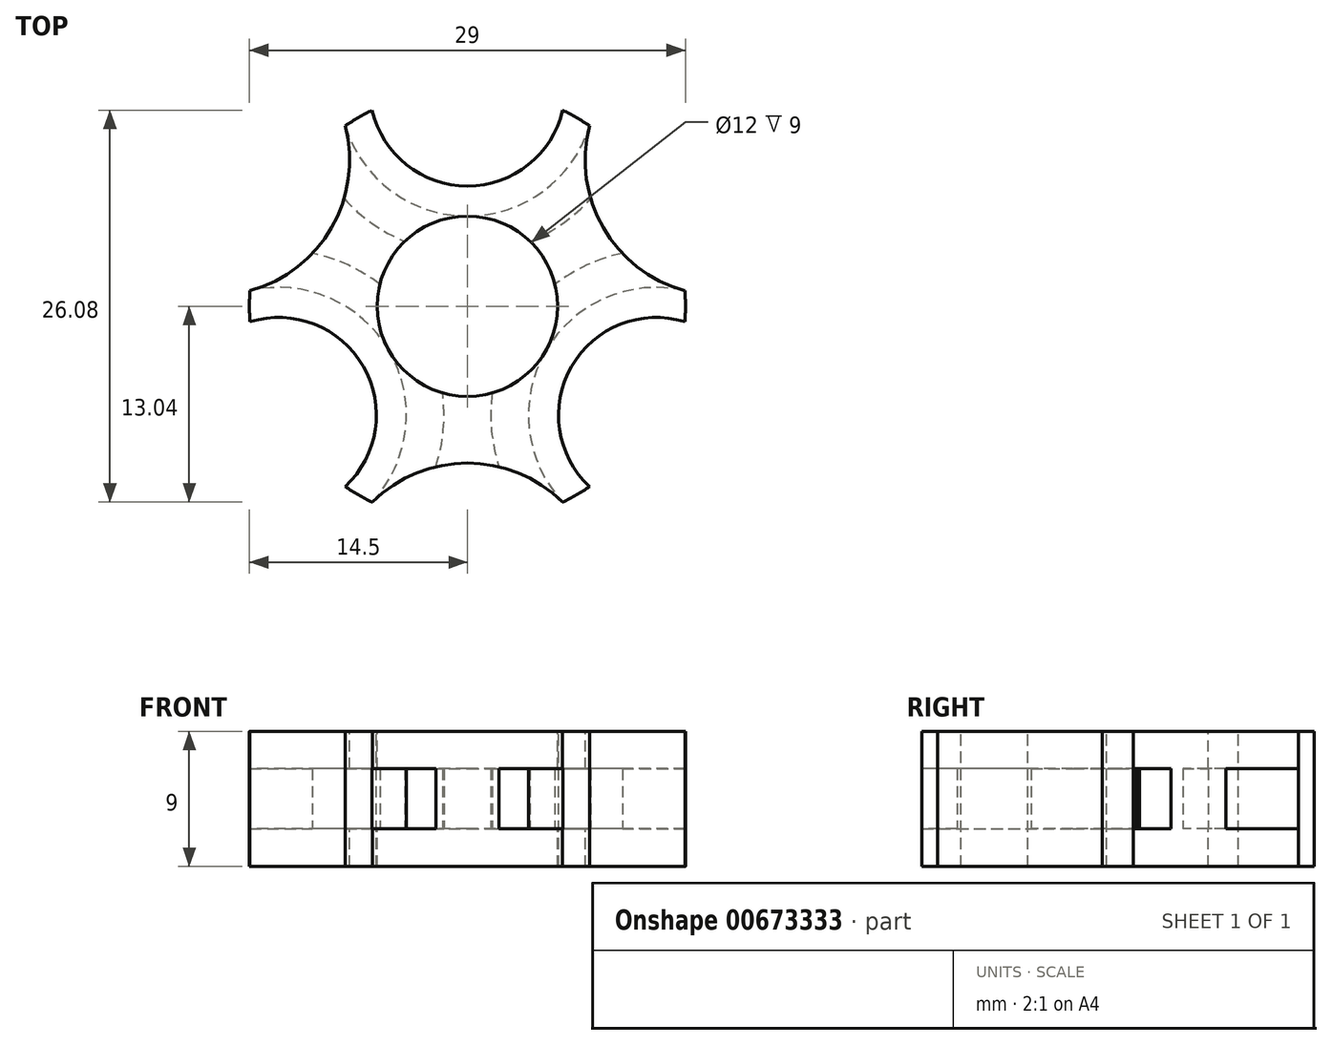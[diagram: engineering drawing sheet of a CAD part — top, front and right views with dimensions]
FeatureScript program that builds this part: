
annotation { "Feature Type Name" : "Feature", "Feature Type Description" : "" }
export const myFeature = defineFeature(function(context is Context, id is Id, definition is map)
    precondition{}
    {
        {
            var Q0;
            Q0=qCreatedBy(makeId("Top.planeOp"),FACE);
            var sketch = newSketch(context, id + "F0", { "sketchPlane" : qUnion([Q0])});
            skCircle(sketch, "E0", {"center": v(0, 0) * mm, "radius": 6 * mm});
            skCircle(sketch, "E1", {"center": v(0, 14.5) * mm, "radius": 8.5 * mm});
            skCircle(sketch, "E2", {"center": v(-12.56, -7.25) * mm, "radius": 8.5 * mm});
            skCircle(sketch, "E3", {"center": v(12.56, -7.25) * mm, "radius": 8.5 * mm});
            skLineSegment(sketch, "E4", {"start": v(0, 14.5) * mm, "end": v(-12.56, -7.25) * mm, "construction": true});
            skLineSegment(sketch, "E5", {"start": v(12.56, -7.25) * mm, "end": v(-12.56, -7.25) * mm, "construction": true});
            skLineSegment(sketch, "E6", {"start": v(0, 14.5) * mm, "end": v(12.56, -7.25) * mm, "construction": true});
            skCircle(sketch, "E7", {"center": v(0, 14.5) * mm, "radius": 6.5 * mm});
            skCircle(sketch, "E8", {"center": v(12.56, -7.25) * mm, "radius": 6.5 * mm});
            skCircle(sketch, "E9", {"center": v(-12.56, -7.25) * mm, "radius": 6.5 * mm});
            skCircle(sketch, "E10", {"center": v(0, 0) * mm, "radius": 14.5 * mm});
            skCircle(sketch, "E11", {"center": v(-16.83, 9.72) * mm, "radius": 9 * mm});
            skCircle(sketch, "E12", {"center": v(16.83, 9.72) * mm, "radius": 9 * mm});
            skCircle(sketch, "E13", {"center": v(0, -19.44) * mm, "radius": 9 * mm});
            skCircle(sketch, "E14", {"center": v(0, 14.5) * mm, "radius": 11 * mm});
            skCircle(sketch, "E15", {"center": v(12.56, -7.25) * mm, "radius": 11 * mm});
            skCircle(sketch, "E16", {"center": v(-12.56, -7.25) * mm, "radius": 11 * mm});
            skSolve(sketch);
        }
        {
            var Q0;
            {var subQ1=sQuery(id+"F0.wireOp",EDGE,"E2");var subQ5=makeQuery(id+"F0.imprint","INTERSECT",VERTEX,{"derivedFrom":[sQuery(id+"F0.wireOp",EDGE,"E0"),subQ1]});Q0=makeQuery(id+"F0.imprint","IMPRINT",FACE,{"disambiguationData":[TD([[makeQuery(id+"F0.imprint","IMPRINT",EDGE,{"disambiguationData":[TD([[subQ5,-1.0]])],"derivedFrom":subQ1}),1.0]])]});}
            var Q1;
            {var subQ1=sQuery(id+"F0.wireOp",EDGE,"E3");var subQ6=makeQuery(id+"F0.imprint","INTERSECT",VERTEX,{"derivedFrom":[sQuery(id+"F0.wireOp",EDGE,"E0"),subQ1]});Q1=makeQuery(id+"F0.imprint","IMPRINT",FACE,{"disambiguationData":[TD([[makeQuery(id+"F0.imprint","IMPRINT",EDGE,{"disambiguationData":[TD([[subQ6,1.0]])],"derivedFrom":subQ1}),1.0]])]});}
            var Q2;
            {var subQ4=sQuery(id+"F0.wireOp",EDGE,"E1");var subQ6=makeQuery(id+"F0.imprint","INTERSECT",VERTEX,{"derivedFrom":[sQuery(id+"F0.wireOp",EDGE,"E0"),subQ4]});Q2=makeQuery(id+"F0.imprint","IMPRINT",FACE,{"disambiguationData":[TD([[makeQuery(id+"F0.imprint","IMPRINT",EDGE,{"disambiguationData":[TD([[subQ6,1.0]])],"derivedFrom":subQ4}),1.0]])]});}
            var Q3;
            {var subQ3=sQuery(id+"F0.wireOp",EDGE,"E14");var subQ7=sQuery(id+"F0.wireOp",EDGE,"E0");var subQ8=makeQuery(id+"F0.imprint","INTERSECT",VERTEX,{"disambiguationData":[OD(0.0)],"derivedFrom":[subQ7,subQ3]});Q3=makeQuery(id+"F0.imprint","IMPRINT",FACE,{"disambiguationData":[TD([[makeQuery(id+"F0.imprint","IMPRINT",EDGE,{"disambiguationData":[TD([[subQ8,-1.0]])],"derivedFrom":subQ7}),-1.0]])]});}
            var Q4;
            {var subQ0=sQuery(id+"F0.wireOp",EDGE,"E14");var subQ1=sQuery(id+"F0.wireOp",EDGE,"E0");var subQ2=makeQuery(id+"F0.imprint","INTERSECT",VERTEX,{"disambiguationData":[OD(0.0)],"derivedFrom":[subQ1,subQ0]});Q4=makeQuery(id+"F0.imprint","IMPRINT",FACE,{"disambiguationData":[TD([[makeQuery(id+"F0.imprint","IMPRINT",EDGE,{"disambiguationData":[TD([[subQ2,1.0]])],"derivedFrom":subQ1}),-1.0]])]});}
            var Q5;
            {var subQ3=sQuery(id+"F0.wireOp",EDGE,"E15");var subQ5=sQuery(id+"F0.wireOp",EDGE,"E0");var subQ6=makeQuery(id+"F0.imprint","INTERSECT",VERTEX,{"disambiguationData":[OD(0.0)],"derivedFrom":[subQ5,subQ3]});Q5=makeQuery(id+"F0.imprint","IMPRINT",FACE,{"disambiguationData":[TD([[makeQuery(id+"F0.imprint","IMPRINT",EDGE,{"disambiguationData":[TD([[subQ6,1.0]])],"derivedFrom":subQ5}),-1.0]])]});}
            var Q6;
            {var subQ5=sQuery(id+"F0.wireOp",EDGE,"E15");var subQ7=sQuery(id+"F0.wireOp",EDGE,"E0");var subQ9=makeQuery(id+"F0.imprint","INTERSECT",VERTEX,{"disambiguationData":[OD(1.0)],"derivedFrom":[subQ7,subQ5]});Q6=makeQuery(id+"F0.imprint","IMPRINT",FACE,{"disambiguationData":[TD([[makeQuery(id+"F0.imprint","IMPRINT",EDGE,{"disambiguationData":[TD([[subQ9,-1.0]])],"derivedFrom":subQ7}),-1.0]])]});}
            var Q7;
            {var subQ0=sQuery(id+"F0.wireOp",EDGE,"E16");var subQ1=sQuery(id+"F0.wireOp",EDGE,"E0");var subQ2=makeQuery(id+"F0.imprint","INTERSECT",VERTEX,{"disambiguationData":[OD(1.0)],"derivedFrom":[subQ1,subQ0]});Q7=makeQuery(id+"F0.imprint","IMPRINT",FACE,{"disambiguationData":[TD([[makeQuery(id+"F0.imprint","IMPRINT",EDGE,{"disambiguationData":[TD([[subQ2,-1.0]])],"derivedFrom":subQ1}),-1.0]])]});}
            var Q8;
            {var subQ5=sQuery(id+"F0.wireOp",EDGE,"E2");var subQ7=sQuery(id+"F0.wireOp",EDGE,"E0");var subQ9=makeQuery(id+"F0.imprint","INTERSECT",VERTEX,{"derivedFrom":[subQ7,subQ5]});Q8=makeQuery(id+"F0.imprint","IMPRINT",FACE,{"disambiguationData":[TD([[makeQuery(id+"F0.imprint","IMPRINT",EDGE,{"disambiguationData":[TD([[subQ9,-1.0]])],"derivedFrom":subQ7}),-1.0]])]});}
            var Q9;
            {var subQ5=sQuery(id+"F0.wireOp",EDGE,"E16");var subQ7=sQuery(id+"F0.wireOp",EDGE,"E0");var subQ8=makeQuery(id+"F0.imprint","INTERSECT",VERTEX,{"disambiguationData":[OD(0.0)],"derivedFrom":[subQ7,subQ5]});Q9=makeQuery(id+"F0.imprint","IMPRINT",FACE,{"disambiguationData":[TD([[makeQuery(id+"F0.imprint","IMPRINT",EDGE,{"disambiguationData":[TD([[subQ8,-1.0]])],"derivedFrom":subQ7}),-1.0]])]});}
            var Q10;
            {var subQ0=sQuery(id+"F0.wireOp",EDGE,"E14");var subQ1=sQuery(id+"F0.wireOp",EDGE,"E0");var subQ2=makeQuery(id+"F0.imprint","INTERSECT",VERTEX,{"disambiguationData":[OD(1.0)],"derivedFrom":[subQ1,subQ0]});Q10=makeQuery(id+"F0.imprint","IMPRINT",FACE,{"disambiguationData":[TD([[makeQuery(id+"F0.imprint","IMPRINT",EDGE,{"disambiguationData":[TD([[subQ2,-1.0]])],"derivedFrom":subQ1}),-1.0]])]});}
            var Q11;
            {var subQ5=sQuery(id+"F0.wireOp",EDGE,"E1");var subQ7=sQuery(id+"F0.wireOp",EDGE,"E0");var subQ8=makeQuery(id+"F0.imprint","INTERSECT",VERTEX,{"derivedFrom":[subQ7,subQ5]});Q11=makeQuery(id+"F0.imprint","IMPRINT",FACE,{"disambiguationData":[TD([[makeQuery(id+"F0.imprint","IMPRINT",EDGE,{"disambiguationData":[TD([[subQ8,-1.0]])],"derivedFrom":subQ7}),-1.0]])]});}
            extrude(context, id + "F1", {"entities" : qUnion([Q0, Q1, Q2, Q3, Q4, Q5, Q6, Q7, Q8, Q9, Q10, Q11]), "oppositeDirection" : true, "depth" : 2.5 * mm, "offsetDistance" : 25 * mm});
        }
        {
            var Q0;
            Q0=makeQuery(id+"F1.opExtrude","SWEPT_BODY",BODY,{"disambiguationData":[OSD([sQuery(id+"F0.wireOp",EDGE,"E0"),sQuery(id+"F0.wireOp",EDGE,"E7"),sQuery(id+"F0.wireOp",EDGE,"E8"),sQuery(id+"F0.wireOp",EDGE,"E9"),sQuery(id+"F0.wireOp",EDGE,"E10"),sQuery(id+"F0.wireOp",EDGE,"E11"),sQuery(id+"F0.wireOp",EDGE,"E12"),sQuery(id+"F0.wireOp",EDGE,"E13")])]});
            transform(context, id + "F2", {"entities" : qUnion([Q0]), "transformType" : TransformType.TRANSLATION_3D, "dx" : 0 * mm, "dy" : 0 * mm, "dz" : 6.5 * mm, "makeCopy" : true});
        }
        {
            var Q0;
            {var subQ4=sQuery(id+"F0.wireOp",EDGE,"E1");var subQ6=makeQuery(id+"F0.imprint","INTERSECT",VERTEX,{"derivedFrom":[sQuery(id+"F0.wireOp",EDGE,"E0"),subQ4]});Q0=makeQuery(id+"F0.imprint","IMPRINT",FACE,{"disambiguationData":[TD([[makeQuery(id+"F0.imprint","IMPRINT",EDGE,{"disambiguationData":[TD([[subQ6,1.0]])],"derivedFrom":subQ4}),1.0]])]});}
            var Q1;
            {var subQ0=sQuery(id+"F0.wireOp",EDGE,"E14");var subQ1=sQuery(id+"F0.wireOp",EDGE,"E0");var subQ2=makeQuery(id+"F0.imprint","INTERSECT",VERTEX,{"disambiguationData":[OD(1.0)],"derivedFrom":[subQ1,subQ0]});Q1=makeQuery(id+"F0.imprint","IMPRINT",FACE,{"disambiguationData":[TD([[makeQuery(id+"F0.imprint","IMPRINT",EDGE,{"disambiguationData":[TD([[subQ2,-1.0]])],"derivedFrom":subQ1}),-1.0]])]});}
            var Q2;
            {var subQ1=sQuery(id+"F0.wireOp",EDGE,"E2");var subQ5=makeQuery(id+"F0.imprint","INTERSECT",VERTEX,{"derivedFrom":[sQuery(id+"F0.wireOp",EDGE,"E0"),subQ1]});Q2=makeQuery(id+"F0.imprint","IMPRINT",FACE,{"disambiguationData":[TD([[makeQuery(id+"F0.imprint","IMPRINT",EDGE,{"disambiguationData":[TD([[subQ5,-1.0]])],"derivedFrom":subQ1}),1.0]])]});}
            var Q3;
            {var subQ0=sQuery(id+"F0.wireOp",EDGE,"E16");var subQ1=sQuery(id+"F0.wireOp",EDGE,"E0");var subQ2=makeQuery(id+"F0.imprint","INTERSECT",VERTEX,{"disambiguationData":[OD(1.0)],"derivedFrom":[subQ1,subQ0]});Q3=makeQuery(id+"F0.imprint","IMPRINT",FACE,{"disambiguationData":[TD([[makeQuery(id+"F0.imprint","IMPRINT",EDGE,{"disambiguationData":[TD([[subQ2,-1.0]])],"derivedFrom":subQ1}),-1.0]])]});}
            var Q4;
            {var subQ1=sQuery(id+"F0.wireOp",EDGE,"E3");var subQ6=makeQuery(id+"F0.imprint","INTERSECT",VERTEX,{"derivedFrom":[sQuery(id+"F0.wireOp",EDGE,"E0"),subQ1]});Q4=makeQuery(id+"F0.imprint","IMPRINT",FACE,{"disambiguationData":[TD([[makeQuery(id+"F0.imprint","IMPRINT",EDGE,{"disambiguationData":[TD([[subQ6,1.0]])],"derivedFrom":subQ1}),1.0]])]});}
            var Q5;
            {var subQ0=sQuery(id+"F0.wireOp",EDGE,"E14");var subQ1=sQuery(id+"F0.wireOp",EDGE,"E0");var subQ2=makeQuery(id+"F0.imprint","INTERSECT",VERTEX,{"disambiguationData":[OD(0.0)],"derivedFrom":[subQ1,subQ0]});Q5=makeQuery(id+"F0.imprint","IMPRINT",FACE,{"disambiguationData":[TD([[makeQuery(id+"F0.imprint","IMPRINT",EDGE,{"disambiguationData":[TD([[subQ2,1.0]])],"derivedFrom":subQ1}),-1.0]])]});}
            extrude(context, id + "F3", {"entities" : qUnion([Q0, Q1, Q2, Q3, Q4, Q5]), "operationType" : NewBodyOperationType.ADD, "depth" : 4 * mm, "offsetDistance" : 25 * mm});
        }
    });
